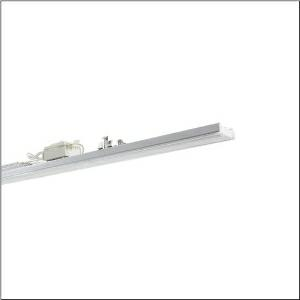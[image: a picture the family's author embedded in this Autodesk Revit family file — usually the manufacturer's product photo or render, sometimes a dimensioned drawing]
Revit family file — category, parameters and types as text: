
# Revit family: licross_11_recessed_ho_51tl12dv4m2m3c
name_source: partatom
category: Lighting Fixtures
units: mm (PartAtom-declared; Revit-internal decimal feet)

## family parameters
Cut with Voids When Loaded = No
Host = Face
Light Source = No
Part Type = Normal
Room Calculation Point = No
Round Connector Dimension = Use Diameter
Shared = No

## types (1)
- --- (1 x LED, 1010 lm, 5.9 W, 4000K)
    Apparent Load = 6 VA
    CIE Flux Codes = 66 91 98 100 100
    Color Rendering = 80
    Color Temperature = 4000K
    Default Elevation = 1800 mm
    Description = Licross 11 Recessed HO, luminaire insert, of sheet steel, coil coated, white, length: 2.250mm, width: 66mm, height: 67mm, LED rated luminous flux: 27.150lm, light colour: 840, SDCM (Standard Deviation of Colour Matching)MacAdam ≤ 2 SDCM (initial), control gear: DALI 2 (for two DALI lines), with plug, 6-pole, with phase selection, for trunking rail, 14-core, mains connection: 220..240V, AC, 50/60Hz, rated input power: 154W, for trunking rail, 14-core, internal wiring halogen-free, for emergency light function, converter,control gear: single battery element, battery: LiFePO4, 9Ah, primary optical cover: cover, of PMMA, light emission: direct distribution, primary light characteristic: symmetric, protection rating (complete): IP40, insulation class (complete): insulation class I (protective earthing), certification: CE, UKCA, protection symbol: D if used in an environment without relevant dust loads with corresponding accessories, impact resistance: IK06, permissible ambient temperature for indoor applications: +5..+35°C, standard: EN 60598-2-22, LABS conformity tested according to VDMA 24364:2018-05, reducing of maximum allowable ambient temperature of 5°C with ceiling mounting, corresponds to IFS (International Featured Standards) requirements for safety and quality in the food industry, The light source and the operating device comply with the requirements of the Ecodesign Regulation (EU) 2019/2020 and are replaceable in accordance with this regulation, packaging unit: 1 piece
    Height = 58 mm
    Lamp = 1 x LED
    Lamp Light Flux = 1010 lm
    Lamp Power = 5.9 W
    Lamp count = 1
    Length = 2250 mm
    Luminous efficacy = 171 lm/W
    Manufacturer = Siteco
    ModVariant = No
    Model = 51TL12DV4M2M3C
    Mounting Place = Ceiling
    Mounting Type = Pendant
    Number of Poles = 1
    OnlyDefault = Yes
    Power Factor = 1
    Product Name = Licross 11 Recessed HO
    Product group = luminaire insert | ceiling pendant
    ProductGroupID = 901
    Protection Class = Protection class I
    Protection Degree = IP 40
    RLX_Detail_Level = 1
    RLX_Emergency_Light_Flux = 0 lm
    RLX_Emergency_Type = 0
    RLX_Emergency_Type_DB = No
    RlxData = <blob elided: 30229 chars, md5=6a478709>
    Socket = socket
    Standby Power = 0 W
    System Light Flux = 1010 lm
    System Power = 6 W
    Type Comments = : emergency light operation: 3 h
    Type Image = l_1296930.jpg
    URL = http://relux.com
    VarID = @adj_089621
    Voltage = 0 V
    Weight = 0.00 kg
    Width = 66 mm

## geometry (parser evidence)
native form markers: Blend x4, Sweep x8
no freeform markers — native parametric forms only
